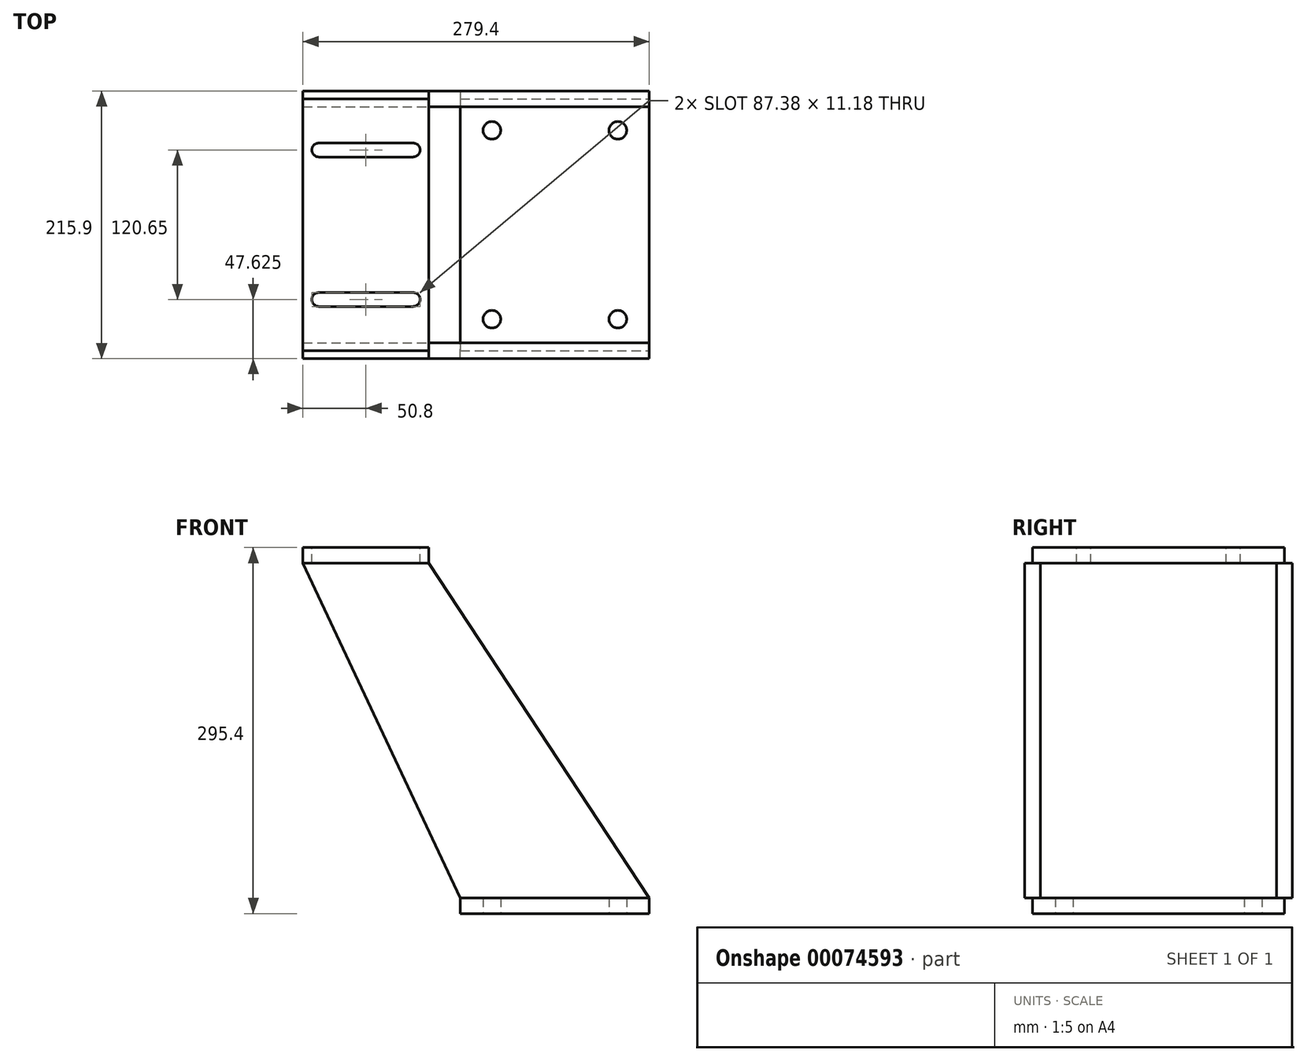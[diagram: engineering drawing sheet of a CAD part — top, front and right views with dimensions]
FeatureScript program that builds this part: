
annotation { "Feature Type Name" : "Feature", "Feature Type Description" : "" }
export const myFeature = defineFeature(function(context is Context, id is Id, definition is map)
    precondition{}
    {
        {
            var Q0;
            Q0=qCreatedBy(makeId("Top.planeOp"),FACE);
            var sketch = newSketch(context, id + "F0", { "sketchPlane" : qUnion([Q0])});
            skLineSegment(sketch, "E0.rect.bottom", {"start": v(-76.2, 101.6) * mm, "end": v(76.2, 101.6) * mm});
            skLineSegment(sketch, "E0.rect.top", {"start": v(-76.2, -101.6) * mm, "end": v(76.2, -101.6) * mm});
            skLineSegment(sketch, "E0.rect.left", {"start": v(-76.2, 101.6) * mm, "end": v(-76.2, -101.6) * mm});
            skLineSegment(sketch, "E0.rect.right", {"start": v(76.2, 101.6) * mm, "end": v(76.2, -101.6) * mm});
            skPoint(sketch, "E0.rect.middle", {"position": v(0, 0) * mm});
            skLineSegment(sketch, "E1.0", {"start": v(-50.8, 76.2) * mm, "end": v(50.8, 76.2) * mm, "construction": true});
            skLineSegment(sketch, "E1.1", {"start": v(-50.8, 76.2) * mm, "end": v(-50.8, -76.2) * mm, "construction": true});
            skLineSegment(sketch, "E1.2", {"start": v(-50.8, -76.2) * mm, "end": v(50.8, -76.2) * mm, "construction": true});
            skLineSegment(sketch, "E1.3", {"start": v(50.8, 76.2) * mm, "end": v(50.8, -76.2) * mm, "construction": true});
            skCircle(sketch, "E2", {"center": v(-50.8, 76.2) * mm, "radius": 7.14 * mm});
            skCircle(sketch, "E3", {"center": v(50.8, 76.2) * mm, "radius": 7.14 * mm});
            skCircle(sketch, "E4", {"center": v(-50.8, -76.2) * mm, "radius": 7.14 * mm});
            skCircle(sketch, "E5", {"center": v(50.8, -76.2) * mm, "radius": 7.14 * mm});
            skSolve(sketch);
        }
        {
            var Q0;
            Q0=qSketchRegion(id+"F0",true);
            extrude(context, id + "F1", {"entities" : qUnion([Q0]), "depth" : 12.7 * mm});
        }
        {
            var Q0;
            Q0=makeQuery(id+"F1.opExtrude","CAP_FACE",FACE,{"disambiguationData":[OSD([sQuery(id+"F0.wireOp",EDGE,"E0.rect.bottom"),sQuery(id+"F0.wireOp",EDGE,"E0.rect.top"),sQuery(id+"F0.wireOp",EDGE,"E0.rect.left"),sQuery(id+"F0.wireOp",EDGE,"E0.rect.right"),sQuery(id+"F0.wireOp",EDGE,"E2"),sQuery(id+"F0.wireOp",EDGE,"E3"),sQuery(id+"F0.wireOp",EDGE,"E4"),sQuery(id+"F0.wireOp",EDGE,"E5")])],"isStart":true});
            cPlane(context, id + "F2", {"entities" : qUnion([Q0]), "cplaneType" : CPlaneType.OFFSET, "offset" : 295.4 * mm, "oppositeDirection" : true, "width" : 152.4 * mm, "height" : 152.4 * mm});
        }
        {
            var Q0;
            Q0=qCreatedBy(id+"F2.planeOp",FACE);
            var sketch = newSketch(context, id + "F3", { "sketchPlane" : qUnion([Q0])});
            skLineSegment(sketch, "E6", {"start": v(0, 185.97) * mm, "end": v(0, -193.47) * mm, "construction": true});
            skLineSegment(sketch, "E7.0", {"start": v(-152.4, 185.97) * mm, "end": v(-152.4, -193.47) * mm, "construction": true});
            skLineSegment(sketch, "E8", {"start": v(107.18, 0) * mm, "end": v(-288.33, 0) * mm, "construction": true});
            skLineSegment(sketch, "E9.rect.bottom", {"start": v(-203.2, 101.6) * mm, "end": v(-101.6, 101.6) * mm});
            skLineSegment(sketch, "E9.rect.top", {"start": v(-203.2, -101.6) * mm, "end": v(-101.6, -101.6) * mm});
            skLineSegment(sketch, "E9.rect.left", {"start": v(-203.2, 101.6) * mm, "end": v(-203.2, -101.6) * mm});
            skLineSegment(sketch, "E9.rect.right", {"start": v(-101.6, 101.6) * mm, "end": v(-101.6, -101.6) * mm});
            skPoint(sketch, "E9.rect.middle", {"position": v(-152.4, 0) * mm});
            skLineSegment(sketch, "E10.0", {"start": v(107.18, 60.33) * mm, "end": v(-288.33, 60.32) * mm, "construction": true});
            skLineSegment(sketch, "E11.0", {"start": v(-190.5, 185.97) * mm, "end": v(-190.5, -193.47) * mm, "construction": true});
            skLineSegment(sketch, "E12.0", {"start": v(-114.3, 185.97) * mm, "end": v(-114.3, -193.47) * mm, "construction": true});
            skLineSegment(sketch, "E13", {"start": v(-190.5, 60.32) * mm, "end": v(-114.3, 60.32) * mm});
            skArc(sketch, "E14.0.startCap", {"start": v(-190.5, 54.74) * mm, "mid": v(-196.09, 60.32) * mm, "end": v(-190.5, 65.91) * mm});
            skArc(sketch, "E14.0.endCap", {"start": v(-114.3, 65.91) * mm, "mid": v(-108.71, 60.32) * mm, "end": v(-114.3, 54.74) * mm});
            skLineSegment(sketch, "E14.0.left", {"start": v(-190.5, 65.91) * mm, "end": v(-114.3, 65.91) * mm});
            skLineSegment(sketch, "E14.0.right", {"start": v(-190.5, 54.74) * mm, "end": v(-114.3, 54.74) * mm});
            skArc(sketch, "E15.MirrorCS", {"start": v(-114.3, -65.91) * mm, "mid": v(-108.71, -60.32) * mm, "end": v(-114.3, -54.74) * mm});
            skArc(sketch, "E16.MirrorCS", {"start": v(-190.5, -54.74) * mm, "mid": v(-196.09, -60.32) * mm, "end": v(-190.5, -65.91) * mm});
            skLineSegment(sketch, "E17.MirrorCS", {"start": v(-190.5, -54.74) * mm, "end": v(-114.3, -54.74) * mm});
            skLineSegment(sketch, "E18.MirrorCS", {"start": v(-190.5, -65.91) * mm, "end": v(-114.3, -65.91) * mm});
            skLineSegment(sketch, "E19.MirrorCS", {"start": v(-190.5, -60.32) * mm, "end": v(-114.3, -60.32) * mm});
            skSolve(sketch);
        }
        {
            var Q0;
            Q0=qSketchRegion(id+"F3",true);
            extrude(context, id + "F4", {"entities" : qUnion([Q0]), "depth" : 12.7 * mm});
        }
        {
            var Q0;
            Q0=makeQuery(id+"F4.opExtrude","SWEPT_FACE",FACE,{"disambiguationData":[OSD([sQuery(id+"F3.wireOp",EDGE,"E9.rect.top")])]});
            var sketch = newSketch(context, id + "F5", { "sketchPlane" : qUnion([Q0])});
            skLineSegment(sketch, "E20.0", {"start": v(76.2, 12.7) * mm, "end": v(-76.2, 12.7) * mm});
            skLineSegment(sketch, "E21.0", {"start": v(203.2, 282.7) * mm, "end": v(101.6, 282.7) * mm});
            skLineSegment(sketch, "E22", {"start": v(203.2, 282.7) * mm, "end": v(76.2, 12.7) * mm});
            skLineSegment(sketch, "E23", {"start": v(101.6, 282.7) * mm, "end": v(-76.2, 12.7) * mm});
            skSolve(sketch);
        }
        {
            var Q0;
            Q0=qSketchRegion(id+"F5",true);
            extrude(context, id + "F6", {"entities" : qUnion([Q0]), "endBound" : BoundingType.SYMMETRIC, "depth" : 12.7 * mm});
        }
        {
            var Q0;
            Q0=makeQuery(id+"F6.opExtrude","SWEPT_BODY",BODY,{"disambiguationData":[OSD([sQuery(id+"F5.wireOp",EDGE,"f1f27c51-49fc-4245-874a-efe3231ee20e.0"),sQuery(id+"F5.wireOp",EDGE,"E20.0"),sQuery(id+"F5.wireOp",EDGE,"P7uxkj9T-qamm-GDIi-5Cy6-n8MuDFCQXTvc"),sQuery(id+"F5.wireOp",EDGE,"06WD7JD2-YMt4-Fifx-PtCd-SJVudk0IbHSt")])]});
            var Q1;
            Q1=qCreatedBy(makeId("Front.planeOp"),FACE);
            mirror(context, id + "F7", {"entities" : qUnion([Q0]), "mirrorPlane" : qUnion([Q1])});
        }
    });
